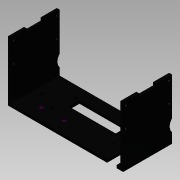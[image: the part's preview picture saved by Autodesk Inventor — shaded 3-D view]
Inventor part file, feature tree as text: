
AUTODESK INVENTOR PART (.ipt)
format: ipt  version: 2015 SP1 (Build 190203100, 203)  size: 209,408 bytes
history: native  units: mm
features: reference x18, extrude x10, sketch x9, plane x1
ambient origin geometry x8: Origin, YZ Plane, XZ Plane, XY Plane, X Axis, Y Axis, Z Axis, Center Point
bodies: Solid1 (feature_tree)
feature tree (38):
  sketch  "Sketch1"  dims[d0=120.812mm d1=51.214111mm]
  extrude  "Extrusion1"  Depth=51.214111mm
  extrude  "Extrusion2"  Depth=63.0mm TaperAngle=0.0deg
  plane  "Work Plane2"
  extrude  "Extrusion3"  Depth=3.0mm
  extrude  "Extrusion4"  [1 undecoded]
  extrude  "Extrusion5"  Depth=3.5mm
  extrude  "Extrusion7"  Depth=3.5mm
  extrude  "Extrusion8"  Depth=17.5mm
  extrude  "Extrusion9"  Depth=10.0mm TaperAngle=0.0deg
  extrude  "Extrusion11"  Depth=10.0mm TaperAngle=0.0deg
  extrude  "Extrusion12"  Depth=10.0mm
  sketch  "Sketch2"  dims[d4=3.0mm d5=0.0mm d6=63.0mm d7=0.0mm]
  reference  "Reference1"
  reference  "Reference2"
  reference  "Reference3"
  reference  "Reference4"
  sketch  "Sketch4"  dims[d8=3.0mm d9=3.0mm]
  sketch  "Sketch6"  dims[d10=114.812mm d11=-18.417445mm]
  reference  "Reference5"
  reference  "Reference6"
  sketch  "Sketch9"  dims[d12=3.5mm d13=3.5mm]
  reference  "Reference8"
  reference  "Reference9"
  reference  "Reference10"
  reference  "Reference11"
  sketch  "Sketch10"  dims[d14=3.5mm d15=3.5mm]
  sketch  "Sketch11"  dims[d16=10.0mm d17=0.0mm d18=17.5mm]
  reference  "Reference13"
  reference  "Reference14"
  reference  "Reference15"
  sketch  "Sketch15"  dims[d19=3.0mm d20=0.0mm d21=10.0mm d22=0.0mm]
  reference  "Reference21"
  sketch  "Sketch16"  dims[d25=200.0mm d26=0.0mm d29=10.0mm d30=0.0mm d31=3.5mm d32=3.5mm d33=2.0mm d34=2.0mm d35=10.0mm d36=0.0mm d37=2.0mm d38=2.0mm d39=90.0deg d47=10.0mm d48=0.0mm d49=10.0mm d50=17.5mm d51=10.0mm d52=0.0mm]
  reference  "Reference22"
  reference  "Reference23"
  reference  "Reference24"
  reference  "Reference25"
note: 1 required parameter value undecoded (feature->parameter linkage not recoverable at this tier; creation-order binding heuristic only, values carry confidence <= 0.55)
